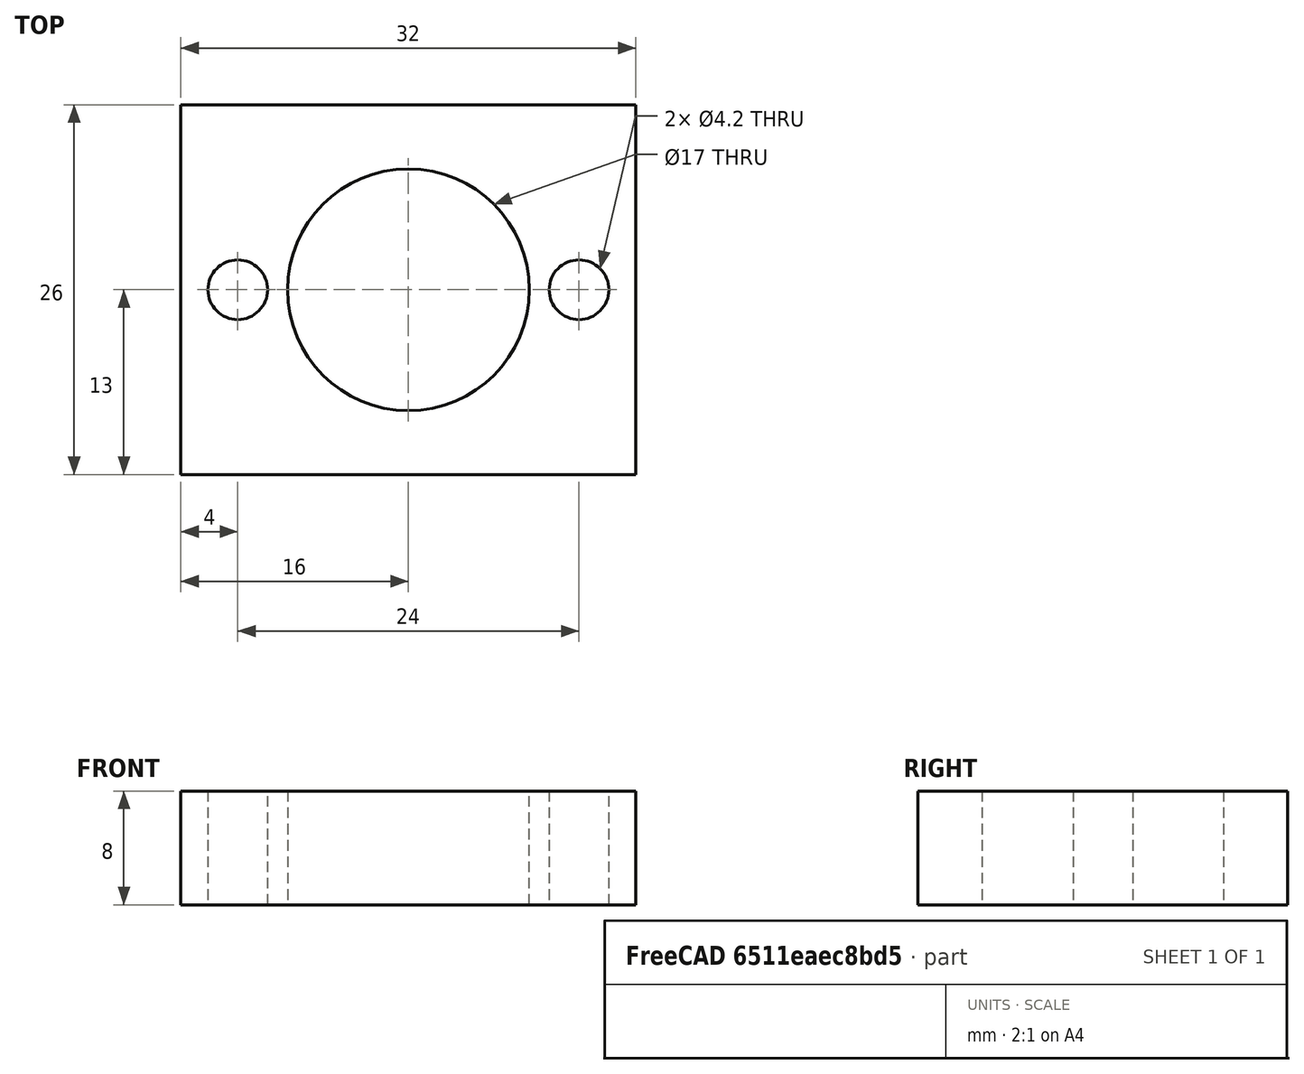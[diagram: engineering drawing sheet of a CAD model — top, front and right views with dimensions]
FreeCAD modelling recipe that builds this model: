
FCSTD DOCUMENT  (FreeCAD 0.21R33771 (Git))
Label: SupportoChiocciolaRicircolo12
License: All rights reserved
LicenseURL: http://en.wikipedia.org/wiki/All_rights_reserved
objects: Sketcher::SketchObject×1, PartDesign::Pad×1, PartDesign::CoordinateSystem×1, PartDesign::Body×1
note: 5 computed .brp shape members not serialized (recipe doc carries the construction recipe); baked Part::Feature solids carry a one-line shape summary decoded from their .brp

FEATURE [Sketcher::SketchObject] Sketch
  FullyConstrained = false
  MapMode = 5
  Support = -> [XY_Plane]
  sketch-geometry (14):
    g0: LineSegment StartX=-16 StartY=13 StartZ=0 EndX=16 EndY=13 EndZ=0
    g1: LineSegment StartX=16 StartY=13 StartZ=0 EndX=16 EndY=-13 EndZ=0
    g2: LineSegment StartX=16 StartY=-13 StartZ=0 EndX=-16 EndY=-13 EndZ=0
    g3: LineSegment StartX=-16 StartY=-13 StartZ=0 EndX=-16 EndY=13 EndZ=0
    g4: Circle CenterX=-2e-16 CenterY=0 CenterZ=0 NormalX=0 NormalY=0 NormalZ=1 AngleXU=0 Radius=8.5
    g5: Circle CenterX=-2e-16 CenterY=0 CenterZ=0 NormalX=0 NormalY=0 NormalZ=1 AngleXU=0 Radius=12
    g6: Circle CenterX=-8.48528 CenterY=8.48528 CenterZ=0 NormalX=0 NormalY=0 NormalZ=1 AngleXU=0 Radius=2.1
    g7: Circle CenterX=8.48528 CenterY=8.48528 CenterZ=0 NormalX=0 NormalY=0 NormalZ=1 AngleXU=0 Radius=2.1
    g8: Circle CenterX=-12 CenterY=0 CenterZ=0 NormalX=0 NormalY=0 NormalZ=1 AngleXU=0 Radius=2.1
    g9: Circle CenterX=8.48528 CenterY=-8.48528 CenterZ=0 NormalX=0 NormalY=0 NormalZ=1 AngleXU=0 Radius=2.1
    g10: Circle CenterX=12 CenterY=0 CenterZ=0 NormalX=0 NormalY=0 NormalZ=1 AngleXU=0 Radius=2.1
    g11: Circle CenterX=-8.48528 CenterY=-8.48528 CenterZ=0 NormalX=0 NormalY=0 NormalZ=1 AngleXU=0 Radius=2.1
    g12: LineSegment StartX=-16.0802 StartY=-16.0802 StartZ=0 EndX=16.7185 EndY=16.7185 EndZ=0
    g13: LineSegment StartX=-17.8445 StartY=17.8445 StartZ=0 EndX=17.734 EndY=-17.734 EndZ=0
  constraints (36):
    c: Coincident(g0,g1)
    c: Coincident(g1,g2)
    c: Coincident(g2,g3)
    c: Coincident(g3,g0)
    c: Horizontal(g0)
    c: Vertical(g1)
    c: Symmetric(g2,g1,g-2)
    c: DistanceX(g2,g2) = 32
    c: Coincident(g4,g-1)
    c: Radius(g4) = 8.5
    c: DistanceY(g3,g3) = 26
    c: Symmetric(g0,g2,g-1)
    c: Coincident(g5,g4)
    c: Radius(g5) = 12
    c: PointOnObject(g6,g5)
    c: PointOnObject(g7,g5)
    c: PointOnObject(g8,g5)
    c: PointOnObject(g9,g5)
    c: PointOnObject(g10,g5)
    c: Radius(g6) = 2.1
    c: Equal(g6,g7)
    c: Equal(g7,g10)
    c: Equal(g10,g9)
    c: Equal(g9,g8)
    c: Equal(g11,g9)
    c: Tangent(g11,g5) = -1.5708
    c: PointOnObject(g4,g13)
    c: PointOnObject(g4,g12)
    c: Angle(g-1,g13) = 2.35619
    c: Angle(g-1,g12) = 0.785398
    c: PointOnObject(g11,g12)
    c: Tangent(g9,g13) = -1.5708
    c: PointOnObject(g8,g-1)
    c: PointOnObject(g6,g13)
    c: PointOnObject(g7,g12)
    c: PointOnObject(g10,g-1)
FEATURE [PartDesign::Pad] Pad
  Direction = (0,0,1)
  Length = 8
  Length2 = 10
  Profile = -> Sketch
  ReferenceAxis = -> Sketch [N_Axis]
  Type = 0
FEATURE [PartDesign::CoordinateSystem] LCS_SupportoChiocciolaRicircolo12
  AttacherType = Attacher::AttachEngine3D
FEATURE [PartDesign::Body] Body
  Group = -> [Sketch,Pad,LCS_SupportoChiocciolaRicircolo12]
  Origin = -> Origin
  Tip = -> Pad
